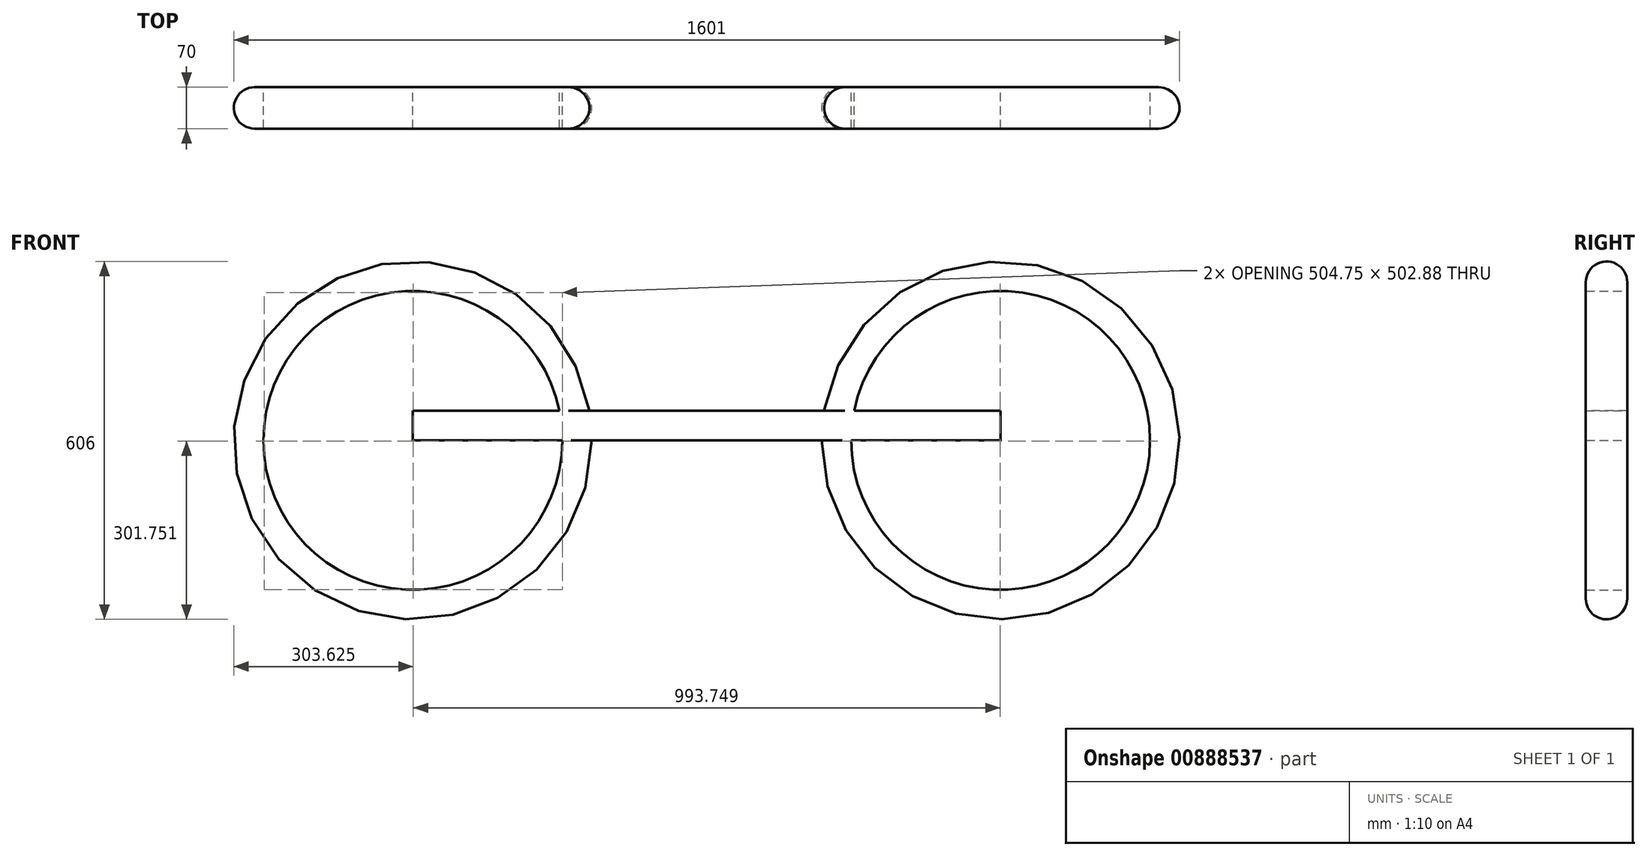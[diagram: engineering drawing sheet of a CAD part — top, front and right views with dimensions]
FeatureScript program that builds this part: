
annotation { "Feature Type Name" : "Feature", "Feature Type Description" : "" }
export const myFeature = defineFeature(function(context is Context, id is Id, definition is map)
    precondition{}
    {
        {
            var Q0;
            Q0=qCreatedBy(makeId("Front.planeOp"),FACE);
            var sketch = newSketch(context, id + "F0", { "sketchPlane" : qUnion([Q0])});
            skCircle(sketch, "E0", {"center": v(0, 0) * mm, "radius": 303 * mm});
            skCircle(sketch, "E1.0", {"center": v(0, 0) * mm, "radius": 253 * mm});
            skSolve(sketch);
        }
        {
            var Q0;
            Q0=qSketchRegion(id+"F0",true);
            extrude(context, id + "F1", {"entities" : qUnion([Q0]), "depth" : 70 * mm, "offsetDistance" : 25 * mm});
        }
        {
            var Q0;
            Q0=makeQuery(id+"F1.opExtrude","CAP_EDGE",EDGE,{"disambiguationData":[OSD([sQuery(id+"F0.wireOp",EDGE,"E0")])],"isStart":false});
            var Q1;
            Q1=makeQuery(id+"F1.opExtrude","CAP_EDGE",EDGE,{"disambiguationData":[OSD([sQuery(id+"F0.wireOp",EDGE,"E0")])],"isStart":true});
            fillet(context, id + "F2", {"entities" : qUnion([Q0, Q1]), "radius" : 35 * mm, "tangentPropagation" : true, "allowEdgeOverflow" : false});
        }
        {
            var Q0;
            Q0=makeQuery(id+"F1.opExtrude","SWEPT_BODY",BODY,{"disambiguationData":[OSD([sQuery(id+"F0.wireOp",EDGE,"E0"),sQuery(id+"F0.wireOp",EDGE,"E1.0")])]});
            transform(context, id + "F3", {"entities" : qUnion([Q0]), "transformType" : TransformType.TRANSLATION_3D, "dx" : 995 * mm, "dy" : 0 * mm, "dz" : 0 * mm, "makeCopy" : true});
        }
        {
            var Q0;
            Q0=qCreatedBy(makeId("Front.planeOp"),FACE);
            var sketch = newSketch(context, id + "F4", { "sketchPlane" : qUnion([Q0])});
            skLineSegment(sketch, "E2.bottom", {"start": v(0, 0) * mm, "end": v(995, 0) * mm});
            skLineSegment(sketch, "E2.top", {"start": v(0, 50) * mm, "end": v(995, 50) * mm});
            skLineSegment(sketch, "E2.left", {"start": v(0, 0) * mm, "end": v(0, 50) * mm});
            skLineSegment(sketch, "E2.right", {"start": v(995, 0) * mm, "end": v(995, 50) * mm});
            skSolve(sketch);
        }
        {
            var Q0;
            Q0=qSketchRegion(id+"F4",true);
            extrude(context, id + "F5", {"entities" : qUnion([Q0]), "operationType" : NewBodyOperationType.ADD, "depth" : 70 * mm, "offsetDistance" : 25 * mm});
        }
    });
